# Revit family: dd82f3ef-5995-4fb4-aad9-62eb7b6e24ff
name_source: partatom
category: Site
revit_build: Autodesk Revit 2016 (Build: 20161004_0715(x64)
units: mm (PartAtom-declared; Revit-internal decimal feet)

## family parameters
Always vertical = Yes
Cut with Voids When Loaded = No
OmniClass Number = 23.10.00.00
OmniClass Title = Site Products
Part Type = Normal
Round Connector Dimension = Use Diameter
Shared = No
Work Plane-Based = No

## types (1)
- Standard
    Color Availability = Standard & Custom
    Description = Precast Concrete Paver
    Manufacturer = Stepstone, Inc
    Manufacturer Fax = 310.217.1424
    Material = Precast Concrete
    Model = 6In x 18In x 2.5In
    Nominal Length = 6"
    Nominal Width = 18"
    Product Line = Pavers
    Product Name = Large Scale CalArc Paver
    Product Page URL = http://www.stepstoneinc.com
    Revit Object Download Link = http://library.smartbim.com
    Subcategory = Large Scale CalArc
    Surface Finish = Integral
    Technical Information = http://www.stepstoneinc.com
    Texture = Sandblast
    Thickness = 2 1/2"
    URL = stepstoneinc.com
    Unit = Concrete - Stepstone - Agave1412
    Warranty = 5 Year Limited
    Weight = 21.00 lb

## geometry (parser evidence)
native form markers: Blend x25, Sweep x5
no freeform markers — native parametric forms only
